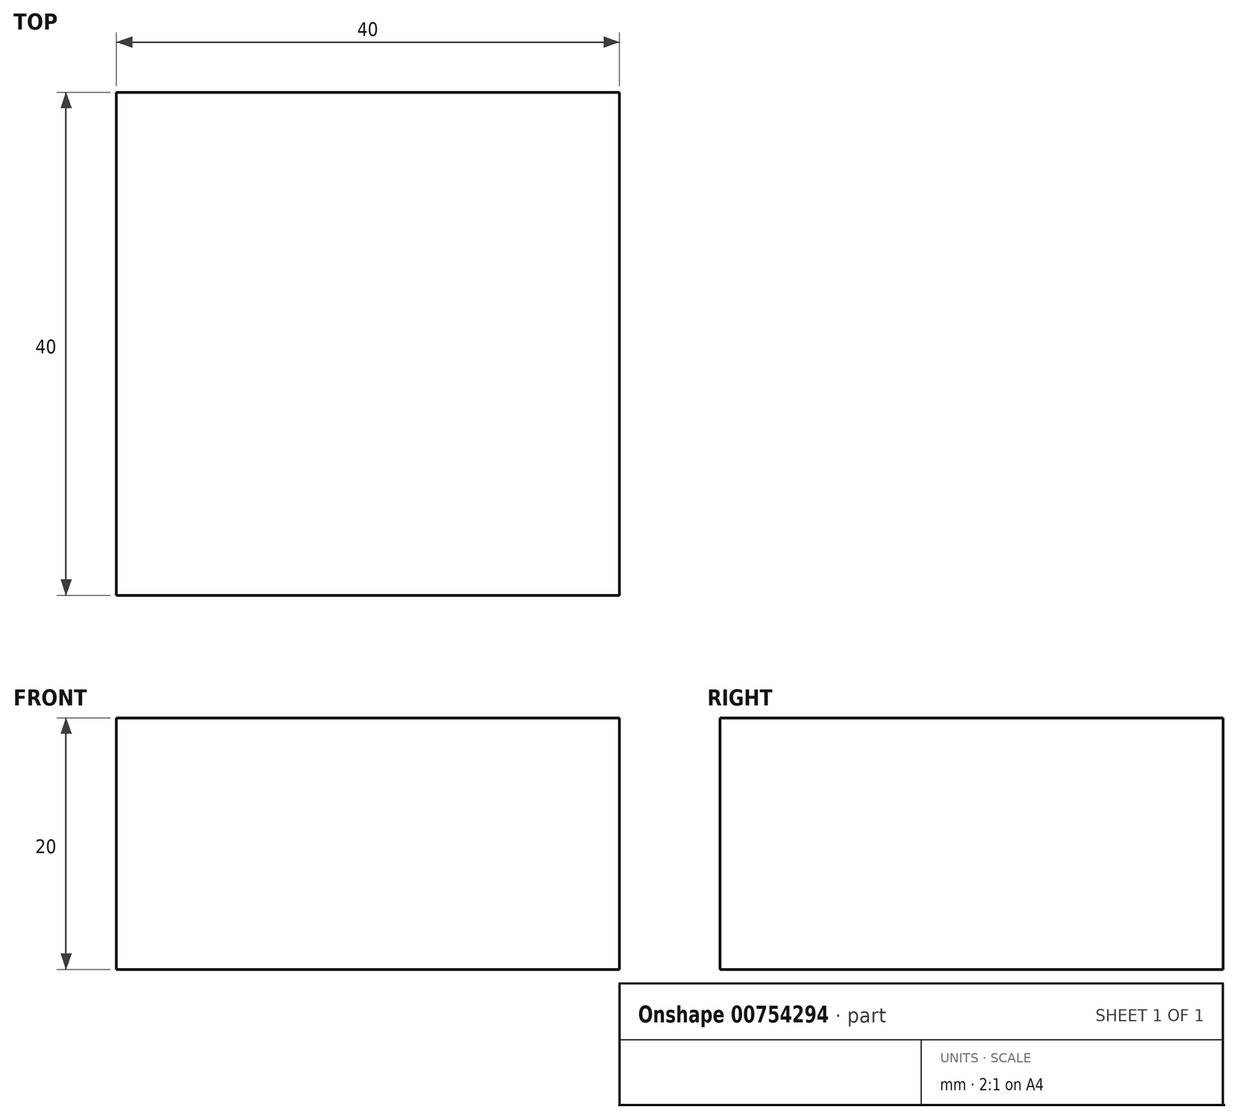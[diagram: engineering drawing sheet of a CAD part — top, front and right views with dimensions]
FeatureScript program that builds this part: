
annotation { "Feature Type Name" : "Feature", "Feature Type Description" : "" }
export const myFeature = defineFeature(function(context is Context, id is Id, definition is map)
    precondition{}
    {
        {
            var Q0;
            Q0=qCreatedBy(makeId("Top.planeOp"),FACE);
            var sketch = newSketch(context, id + "F0", { "sketchPlane" : qUnion([Q0])});
            skLineSegment(sketch, "E0.bottom", {"start": v(20, 20) * mm, "end": v(-20, 20) * mm});
            skLineSegment(sketch, "E0.top", {"start": v(20, -20) * mm, "end": v(-20, -20) * mm});
            skLineSegment(sketch, "E0.left", {"start": v(20, 20) * mm, "end": v(20, -20) * mm});
            skLineSegment(sketch, "E0.right", {"start": v(-20, 20) * mm, "end": v(-20, -20) * mm});
            skPoint(sketch, "E0.middle", {"position": v(0, 0) * mm});
            skSolve(sketch);
        }
        {
            var Q0;
            Q0=makeQuery(id+"F0.imprint","IMPRINT",FACE,{"disambiguationData":[TD([[makeQuery(id+"F0.imprint","IMPRINT",EDGE,{"derivedFrom":sQuery(id+"F0.wireOp",EDGE,"E0.bottom")}),1.0]])]});
            extrude(context, id + "F1", {"entities" : qUnion([Q0]), "depth" : 20 * mm, "offsetDistance" : 25 * mm});
        }
    });
